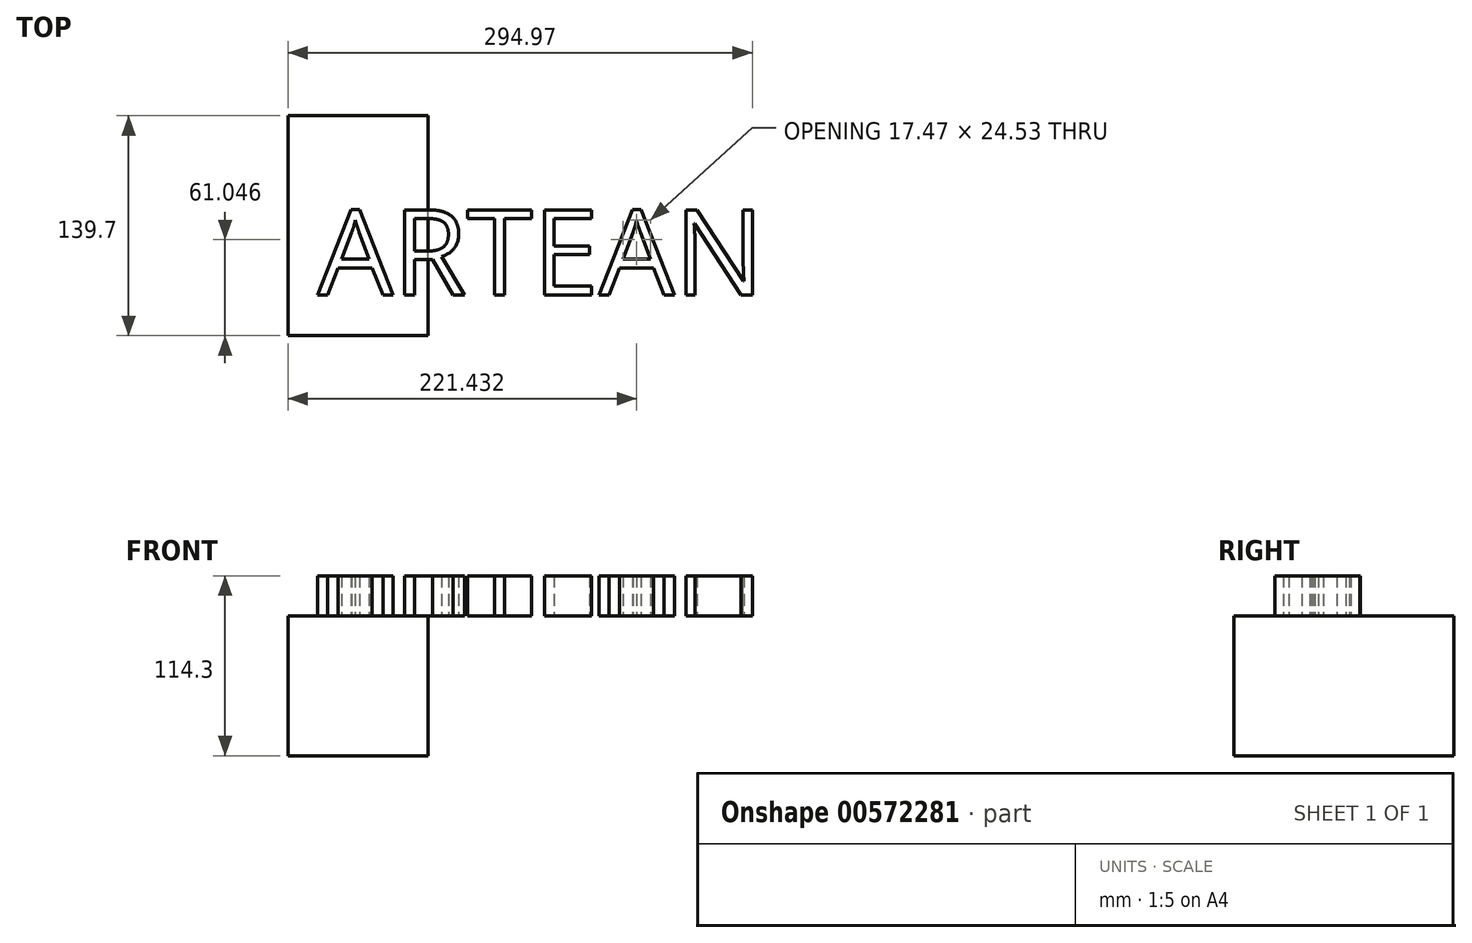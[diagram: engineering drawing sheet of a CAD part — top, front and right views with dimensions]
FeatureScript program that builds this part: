
annotation { "Feature Type Name" : "Feature", "Feature Type Description" : "" }
export const myFeature = defineFeature(function(context is Context, id is Id, definition is map)
    precondition{}
    {
        {
            var Q0;
            Q0=qCreatedBy(makeId("Front.planeOp"),FACE);
            var sketch = newSketch(context, id + "F0", { "sketchPlane" : qUnion([Q0])});
            skLineSegment(sketch, "E0.bottom", {"start": v(-16.72, 79.03) * mm, "end": v(72.18, 79.03) * mm});
            skLineSegment(sketch, "E0.top", {"start": v(-16.72, -9.87) * mm, "end": v(72.18, -9.87) * mm});
            skLineSegment(sketch, "E0.left", {"start": v(-16.72, 79.03) * mm, "end": v(-16.72, -9.87) * mm});
            skLineSegment(sketch, "E0.right", {"start": v(72.18, 79.03) * mm, "end": v(72.18, -9.87) * mm});
            skSolve(sketch);
        }
        {
            var Q0;
            Q0 = qSketchRegion(id + "F0", true);
            extrude(context, id + "F1", {"entities" : qUnion([Q0]), "depth" : 139.7 * mm, "offsetDistance" : 25.4 * mm});
        }
        {
            var Q0;
            Q0=makeQuery(id+"F1.opExtrude","SWEPT_FACE",FACE,{"disambiguationData":[OSD([sQuery(id+"F0.wireOp",EDGE,"E0.bottom")])]});
            var sketch = newSketch(context, id + "F2", { "sketchPlane" : qUnion([Q0])});
            skText(sketch, "E1", { "text": "ARTEAN", "fontName": "OpenSans-Regular.ttf"});
            const initialGuessF2  = {"E1": [0.00215, -0.11375, 1, 0, 0.05448]};
            skSetInitialGuess(sketch, initialGuessF2);
            skSolve(sketch);
        }
        {
            var Q0;
            Q0 = qSketchRegion(id + "F2", true);
            extrude(context, id + "F3", {"entities" : qUnion([Q0]), "operationType" : NewBodyOperationType.ADD, "depth" : 25.4 * mm, "offsetDistance" : 25.4 * mm});
        }
    });
